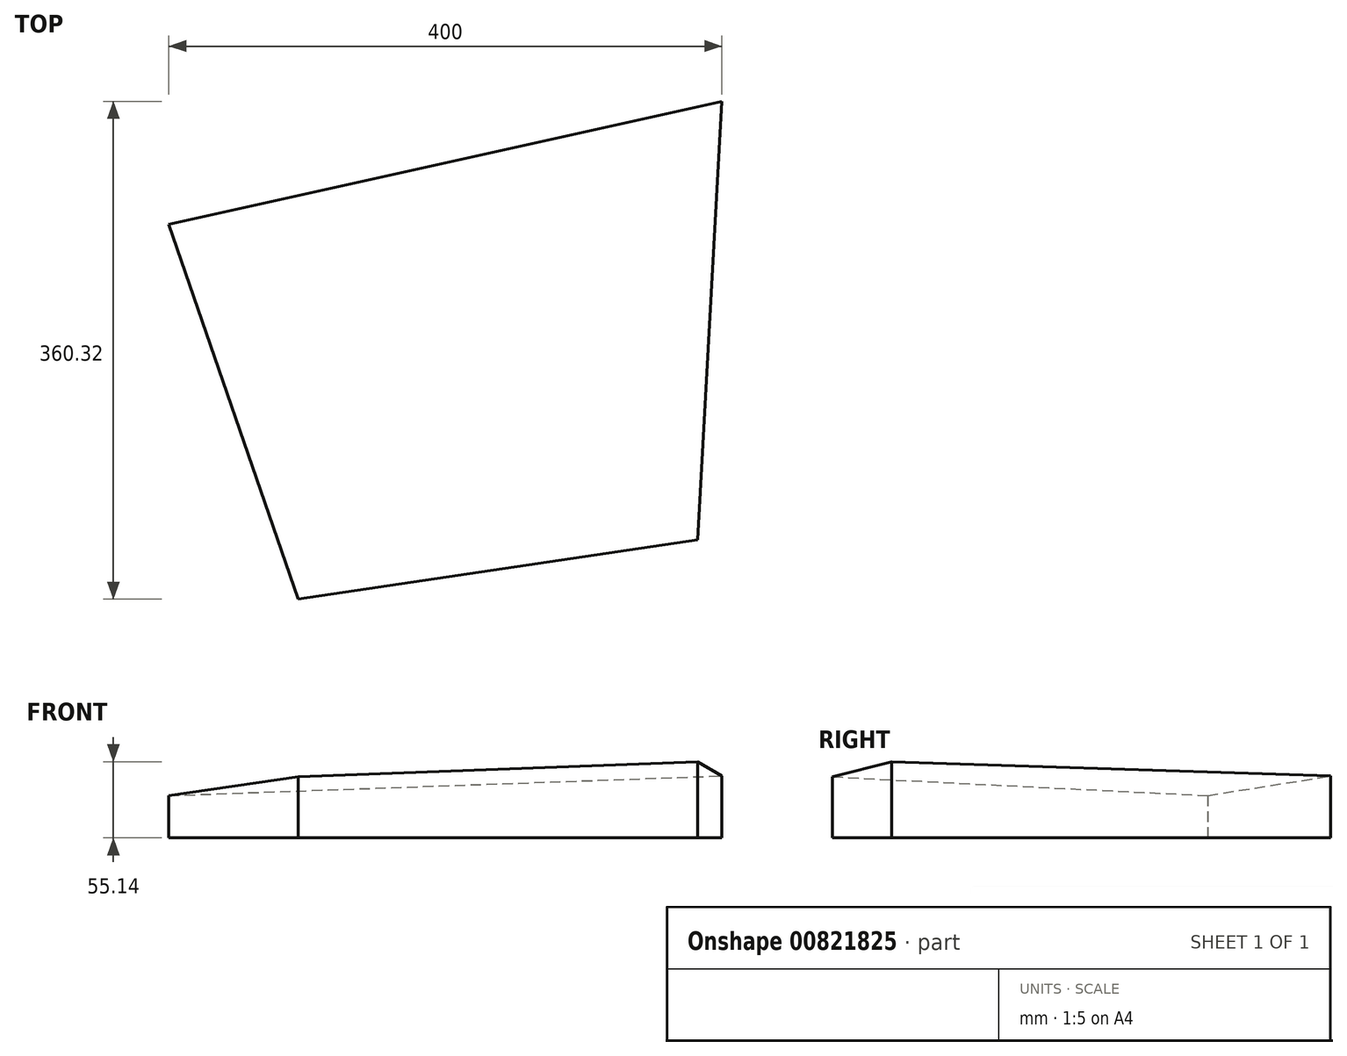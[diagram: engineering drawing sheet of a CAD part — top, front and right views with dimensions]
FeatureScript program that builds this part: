
annotation { "Feature Type Name" : "Feature", "Feature Type Description" : "" }
export const myFeature = defineFeature(function(context is Context, id is Id, definition is map)
    precondition{}
    {
        {
            var Q0;
            Q0=qCreatedBy(makeId("Top.planeOp"),FACE);
            var sketch = newSketch(context, id + "F0", { "sketchPlane" : qUnion([Q0])});
            skLineSegment(sketch, "E0", {"start": v(0, 0) * mm, "end": v(-93.65, 271.43) * mm});
            skLineSegment(sketch, "E1", {"start": v(-93.65, 271.43) * mm, "end": v(306.35, 360.32) * mm});
            skLineSegment(sketch, "E2", {"start": v(306.35, 360.32) * mm, "end": v(288.89, 42.86) * mm});
            skLineSegment(sketch, "E3", {"start": v(288.89, 42.86) * mm, "end": v(0, 0) * mm});
            skSolve(sketch);
        }
        {
            var Q0;
            Q0 = qSketchRegion(id + "F0", true);
            extrude(context, id + "F1", {"entities" : qUnion([Q0]), "depth" : 60 * mm, "offsetDistance" : 25 * mm});
        }
        {
            var Q0;
            Q0=qCreatedBy(makeId("Front.planeOp"),FACE);
            var sketch = newSketch(context, id + "F2", { "sketchPlane" : qUnion([Q0])});
            skLineSegment(sketch, "E4", {"start": v(-94.74, 40) * mm, "end": v(325.08, 58.21) * mm, "construction": true});
            skSolve(sketch);
        }
        {
            var Q0;
            Q0=sQuery(id+"F2.wireOp",EDGE,"E4");
            cPlane(context, id + "F3", {"entities" : qUnion([Q0]), "cplaneType" : CPlaneType.LINE_ANGLE, "offset" : 25 * mm, "angle" : 88 * degree, "width" : 150 * mm, "height" : 150 * mm});
        }
        {
            var Q0;
            Q0=qCreatedBy(id+"F3.planeOp",FACE);
            var sketch = newSketch(context, id + "F4", { "sketchPlane" : qUnion([Q0])});
            skLineSegment(sketch, "E5.bottom", {"start": v(-107.94, -148.57) * mm, "end": v(432.6, -148.57) * mm});
            skLineSegment(sketch, "E5.top", {"start": v(-107.94, 407.37) * mm, "end": v(432.6, 407.37) * mm});
            skLineSegment(sketch, "E5.left", {"start": v(-107.94, -148.57) * mm, "end": v(-107.94, 407.37) * mm});
            skLineSegment(sketch, "E5.right", {"start": v(432.6, -148.57) * mm, "end": v(432.6, 407.37) * mm});
            skSolve(sketch);
        }
        {
            var Q0;
            Q0 = qSketchRegion(id + "F4", true);
            extrude(context, id + "F5", {"entities" : qUnion([Q0]), "operationType" : NewBodyOperationType.REMOVE, "depth" : 60 * mm, "offsetDistance" : 25 * mm});
        }
    });
